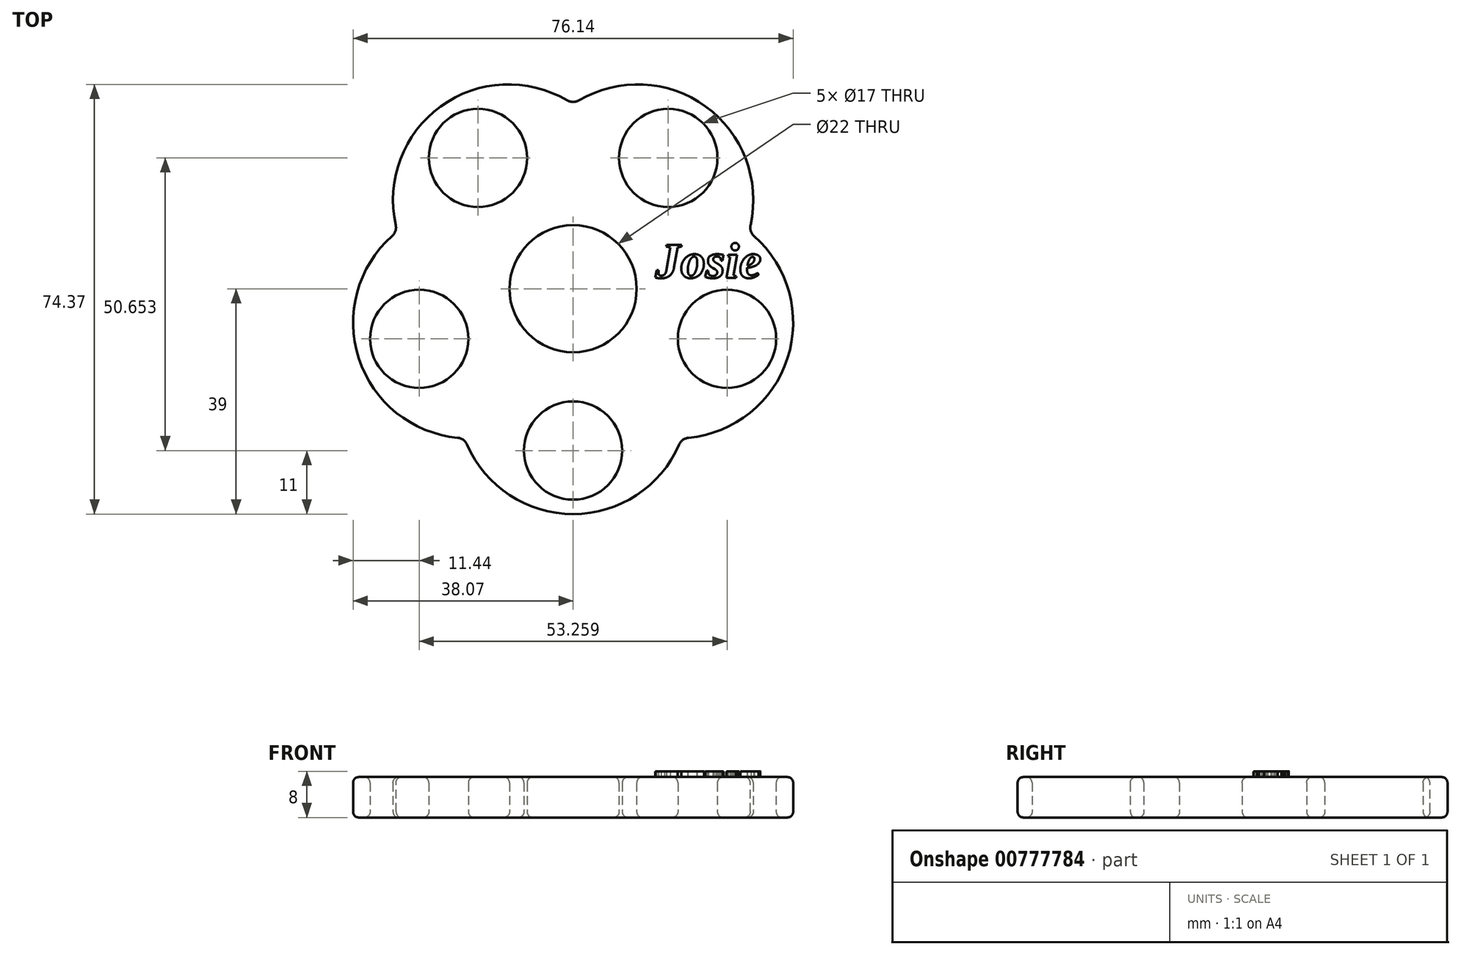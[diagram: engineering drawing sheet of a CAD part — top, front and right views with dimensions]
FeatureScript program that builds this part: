
annotation { "Feature Type Name" : "Feature", "Feature Type Description" : "" }
export const myFeature = defineFeature(function(context is Context, id is Id, definition is map)
    precondition{}
    {
        {
            var Q0;
            Q0=qCreatedBy(makeId("Top.planeOp"),FACE);
            var sketch = newSketch(context, id + "F0", { "sketchPlane" : qUnion([Q0])});
            skCircle(sketch, "E0.cCircle", {"center": v(0, 0) * mm, "radius": 19 * mm, "construction": true});
            skPoint(sketch, "E0.0.midPoint", {"position": v(11.17, 15.37) * mm});
            skArc(sketch, "E1", {"start": v(0, 31.96) * mm, "mid": v(-22.92, 31.55) * mm, "end": v(-30.4, 9.88) * mm});
            skArc(sketch, "E2", {"start": v(30.4, 9.88) * mm, "mid": v(22.92, 31.55) * mm, "end": v(0, 31.96) * mm});
            skArc(sketch, "E3", {"start": v(18.79, -25.86) * mm, "mid": v(37.1, -12.05) * mm, "end": v(30.4, 9.88) * mm});
            skArc(sketch, "E4", {"start": v(-18.79, -25.86) * mm, "mid": v(0, -39) * mm, "end": v(18.79, -25.86) * mm});
            skArc(sketch, "E5", {"start": v(-30.4, 9.88) * mm, "mid": v(-37.1, -12.05) * mm, "end": v(-18.79, -25.86) * mm});
            skCircle(sketch, "E6", {"center": v(0, 0) * mm, "radius": 31.96 * mm, "construction": true});
            skCircle(sketch, "E7", {"center": v(0, 0) * mm, "radius": 11 * mm});
            skCircle(sketch, "E8", {"center": v(-16.46, 22.65) * mm, "radius": 8.5 * mm});
            skCircle(sketch, "E9", {"center": v(16.46, 22.65) * mm, "radius": 8.5 * mm});
            skCircle(sketch, "E10", {"center": v(26.63, -8.65) * mm, "radius": 8.5 * mm});
            skCircle(sketch, "E11", {"center": v(0, -28) * mm, "radius": 8.5 * mm});
            skCircle(sketch, "E12", {"center": v(-26.63, -8.65) * mm, "radius": 8.5 * mm});
            skCircle(sketch, "E13", {"center": v(0, 0) * mm, "radius": 28 * mm, "construction": true});
            skLineSegment(sketch, "E14", {"start": v(0, 0) * mm, "end": v(0, 61.86) * mm, "construction": true});
            skLineSegment(sketch, "E15", {"start": v(0, 0) * mm, "end": v(34.94, 48.1) * mm, "construction": true});
            skLineSegment(sketch, "E16", {"start": v(0, 0) * mm, "end": v(70.3, -22.84) * mm, "construction": true});
            skLineSegment(sketch, "E17", {"start": v(0, 0) * mm, "end": v(0, -36.5) * mm, "construction": true});
            skLineSegment(sketch, "E18", {"start": v(0, 0) * mm, "end": v(-61.86, -20.1) * mm, "construction": true});
            skLineSegment(sketch, "E19", {"start": v(0, 0) * mm, "end": v(-31.6, 43.5) * mm, "construction": true});
            skSolve(sketch);
        }
        {
            var Q0;
            Q0=qSketchRegion(id+"F0",true);
            extrude(context, id + "F1", {"entities" : qUnion([Q0]), "depth" : 7 * mm, "offsetDistance" : 25.4 * mm});
        }
        {
            var Q0;
            Q0=makeQuery(id+"F1.opExtrude","SWEPT_EDGE",EDGE,{"disambiguationData":[OSD([sQuery(id+"F0.wireOp",EDGE,"E3"),sQuery(id+"F0.wireOp",EDGE,"E4")])]});
            var Q1;
            Q1=makeQuery(id+"F1.opExtrude","SWEPT_EDGE",EDGE,{"disambiguationData":[OSD([sQuery(id+"F0.wireOp",EDGE,"E2"),sQuery(id+"F0.wireOp",EDGE,"E3")])]});
            var Q2;
            Q2=makeQuery(id+"F1.opExtrude","SWEPT_EDGE",EDGE,{"disambiguationData":[OSD([sQuery(id+"F0.wireOp",EDGE,"E1"),sQuery(id+"F0.wireOp",EDGE,"E2")])]});
            var Q3;
            Q3=makeQuery(id+"F1.opExtrude","SWEPT_EDGE",EDGE,{"disambiguationData":[OSD([sQuery(id+"F0.wireOp",EDGE,"E1"),sQuery(id+"F0.wireOp",EDGE,"E5")])]});
            var Q4;
            Q4=makeQuery(id+"F1.opExtrude","SWEPT_EDGE",EDGE,{"disambiguationData":[OSD([sQuery(id+"F0.wireOp",EDGE,"E4"),sQuery(id+"F0.wireOp",EDGE,"E5")])]});
            fillet(context, id + "F2", {"entities" : qUnion([Q0, Q1, Q2, Q3, Q4]), "radius" : 2 * mm, "tangentPropagation" : true, "allowEdgeOverflow" : false});
        }
        {
            var Q0;
            Q0=makeQuery(id+"F1.opExtrude","CAP_FACE",FACE,{"disambiguationData":[OSD([sQuery(id+"F0.wireOp",EDGE,"E1"),sQuery(id+"F0.wireOp",EDGE,"E2"),sQuery(id+"F0.wireOp",EDGE,"E3"),sQuery(id+"F0.wireOp",EDGE,"E4"),sQuery(id+"F0.wireOp",EDGE,"E5"),sQuery(id+"F0.wireOp",EDGE,"E7"),sQuery(id+"F0.wireOp",EDGE,"E8"),sQuery(id+"F0.wireOp",EDGE,"E9"),sQuery(id+"F0.wireOp",EDGE,"E10"),sQuery(id+"F0.wireOp",EDGE,"E11"),sQuery(id+"F0.wireOp",EDGE,"E12")])],"isStart":false});
            var Q1;
            Q1=makeQuery(id+"F1.opExtrude","CAP_FACE",FACE,{"disambiguationData":[OSD([sQuery(id+"F0.wireOp",EDGE,"E1"),sQuery(id+"F0.wireOp",EDGE,"E2"),sQuery(id+"F0.wireOp",EDGE,"E3"),sQuery(id+"F0.wireOp",EDGE,"E4"),sQuery(id+"F0.wireOp",EDGE,"E5"),sQuery(id+"F0.wireOp",EDGE,"E7"),sQuery(id+"F0.wireOp",EDGE,"E8"),sQuery(id+"F0.wireOp",EDGE,"E9"),sQuery(id+"F0.wireOp",EDGE,"E10"),sQuery(id+"F0.wireOp",EDGE,"E11"),sQuery(id+"F0.wireOp",EDGE,"E12")])],"isStart":true});
            fillet(context, id + "F3", {"entities" : qUnion([Q0, Q1]), "radius" : 1 * mm, "tangentPropagation" : true, "allowEdgeOverflow" : false});
        }
        {
            var Q0;
            Q0=makeQuery(id+"F1.opExtrude","CAP_FACE",FACE,{"disambiguationData":[OSD([sQuery(id+"F0.wireOp",EDGE,"E1"),sQuery(id+"F0.wireOp",EDGE,"E2"),sQuery(id+"F0.wireOp",EDGE,"E3"),sQuery(id+"F0.wireOp",EDGE,"E4"),sQuery(id+"F0.wireOp",EDGE,"E5"),sQuery(id+"F0.wireOp",EDGE,"E7"),sQuery(id+"F0.wireOp",EDGE,"E8"),sQuery(id+"F0.wireOp",EDGE,"E9"),sQuery(id+"F0.wireOp",EDGE,"E10"),sQuery(id+"F0.wireOp",EDGE,"E11"),sQuery(id+"F0.wireOp",EDGE,"E12")])],"isStart":false});
            var sketch = newSketch(context, id + "F4", { "sketchPlane" : qUnion([Q0])});
            skText(sketch, "E20", { "text": "Josie", "fontName": "Tinos-BoldItalic.ttf"});
            const initialGuessF4  = {"E20": [0.01423, 0.0019, 1, 0, 0.00626]};
            skSetInitialGuess(sketch, initialGuessF4);
            skSolve(sketch);
        }
        {
            var Q0;
            Q0=qSketchRegion(id+"F4",true);
            extrude(context, id + "F5", {"entities" : qUnion([Q0]), "operationType" : NewBodyOperationType.ADD, "depth" : 1 * mm, "offsetDistance" : 25 * mm});
        }
    });
